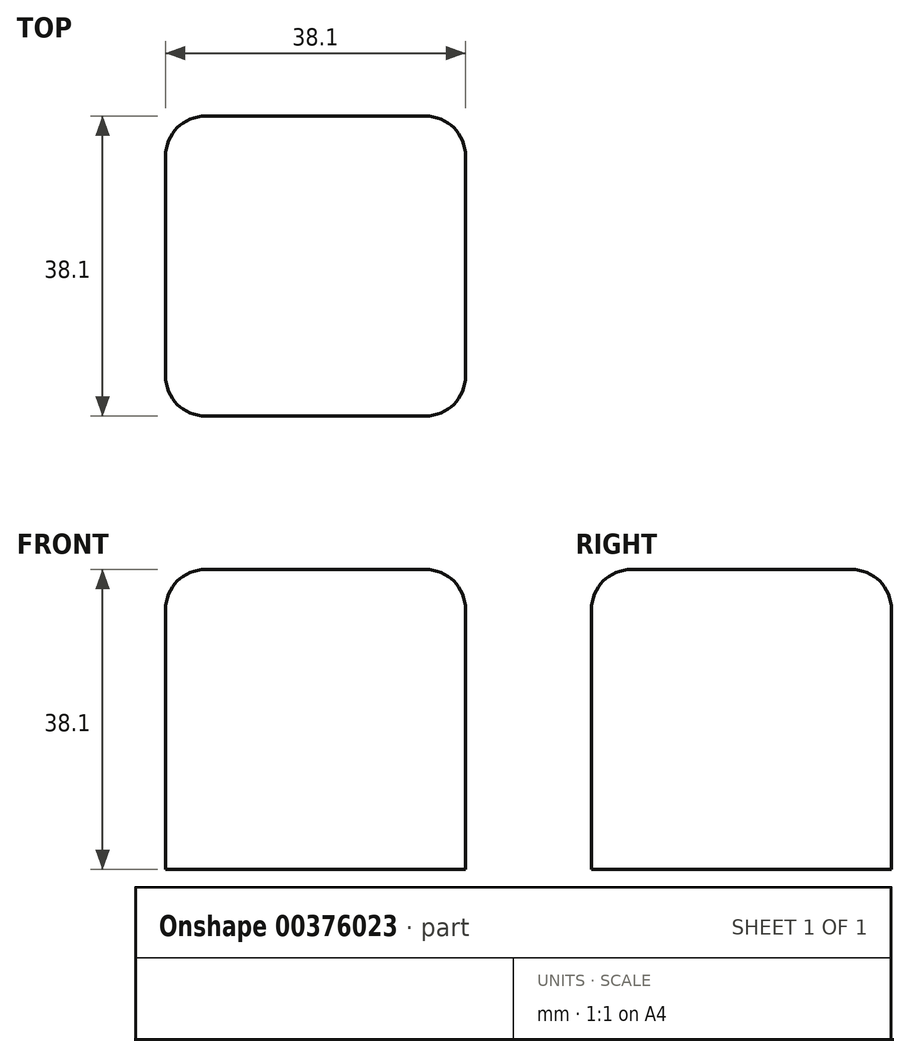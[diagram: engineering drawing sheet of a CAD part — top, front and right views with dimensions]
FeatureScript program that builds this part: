
annotation { "Feature Type Name" : "Feature", "Feature Type Description" : "" }
export const myFeature = defineFeature(function(context is Context, id is Id, definition is map)
    precondition{}
    {
        {
            var Q0;
            Q0=qCreatedBy(makeId("Top.planeOp"),FACE);
            var sketch = newSketch(context, id + "F0", { "sketchPlane" : qUnion([Q0])});
            skLineSegment(sketch, "E0.bottom", {"start": v(19.05, -19.05) * mm, "end": v(-19.05, -19.05) * mm});
            skLineSegment(sketch, "E0.top", {"start": v(19.05, 19.05) * mm, "end": v(-19.05, 19.05) * mm});
            skLineSegment(sketch, "E0.left", {"start": v(19.05, -19.05) * mm, "end": v(19.05, 19.05) * mm});
            skLineSegment(sketch, "E0.right", {"start": v(-19.05, -19.05) * mm, "end": v(-19.05, 19.05) * mm});
            skPoint(sketch, "E0.middle", {"position": v(0, 0) * mm});
            skSolve(sketch);
        }
        {
            var Q0;
            Q0=makeQuery(id+"F0.imprint","IMPRINT",FACE,{"disambiguationData":[TD([[makeQuery(id+"F0.imprint","IMPRINT",EDGE,{"derivedFrom":sQuery(id+"F0.wireOp",EDGE,"E0.bottom")}),-1.0]])]});
            var sketch = newSketch(context, id + "F1", { "sketchPlane" : qUnion([Q0])});
            skSolve(sketch);
        }
        {
            var Q0;
            Q0=makeQuery(id+"F1.imprint","IMPRINT",FACE,{"disambiguationData":[TD([[makeQuery(id+"F1.imprint","IMPRINT",EDGE,{"derivedFrom":makeQuery(id+"F0.imprint","IMPRINT",EDGE,{"derivedFrom":sQuery(id+"F0.wireOp",EDGE,"E0.bottom")})}),-1.0]])]});
            extrude(context, id + "F2", {"entities" : qUnion([Q0]), "endBound" : BoundingType.SYMMETRIC, "depth" : 38.1 * mm});
        }
        {
            var Q0;
            Q0=makeQuery(id+"F2.opExtrude","CAP_EDGE",EDGE,{"disambiguationData":[OSD([sQuery(id+"F0.wireOp",EDGE,"E0.bottom")])],"isStart":false});
            var Q1;
            Q1=makeQuery(id+"F2.opExtrude","CAP_EDGE",EDGE,{"disambiguationData":[OSD([sQuery(id+"F0.wireOp",EDGE,"E0.left")])],"isStart":false});
            var Q2;
            Q2=makeQuery(id+"F2.opExtrude","CAP_EDGE",EDGE,{"disambiguationData":[OSD([sQuery(id+"F0.wireOp",EDGE,"E0.top")])],"isStart":false});
            var Q3;
            Q3=makeQuery(id+"F2.opExtrude","CAP_EDGE",EDGE,{"disambiguationData":[OSD([sQuery(id+"F0.wireOp",EDGE,"E0.right")])],"isStart":false});
            var Q4;
            Q4=makeQuery(id+"F2.opExtrude","SWEPT_EDGE",EDGE,{"disambiguationData":[OSD([sQuery(id+"F0.wireOp",EDGE,"E0.bottom"),sQuery(id+"F0.wireOp",EDGE,"E0.left")])]});
            var Q5;
            Q5=makeQuery(id+"F2.opExtrude","SWEPT_EDGE",EDGE,{"disambiguationData":[OSD([sQuery(id+"F0.wireOp",EDGE,"E0.bottom"),sQuery(id+"F0.wireOp",EDGE,"E0.right")])]});
            var Q6;
            Q6=makeQuery(id+"F2.opExtrude","SWEPT_EDGE",EDGE,{"disambiguationData":[OSD([sQuery(id+"F0.wireOp",EDGE,"E0.top"),sQuery(id+"F0.wireOp",EDGE,"E0.left")])]});
            var Q7;
            Q7=makeQuery(id+"F2.opExtrude","SWEPT_EDGE",EDGE,{"disambiguationData":[OSD([sQuery(id+"F0.wireOp",EDGE,"E0.top"),sQuery(id+"F0.wireOp",EDGE,"E0.right")])]});
            fillet(context, id + "F3", {"entities" : qUnion([Q0, Q1, Q2, Q3, Q4, Q5, Q6, Q7]), "radius" : 5.08 * mm, "tangentPropagation" : true, "allowEdgeOverflow" : false});
        }
    });
